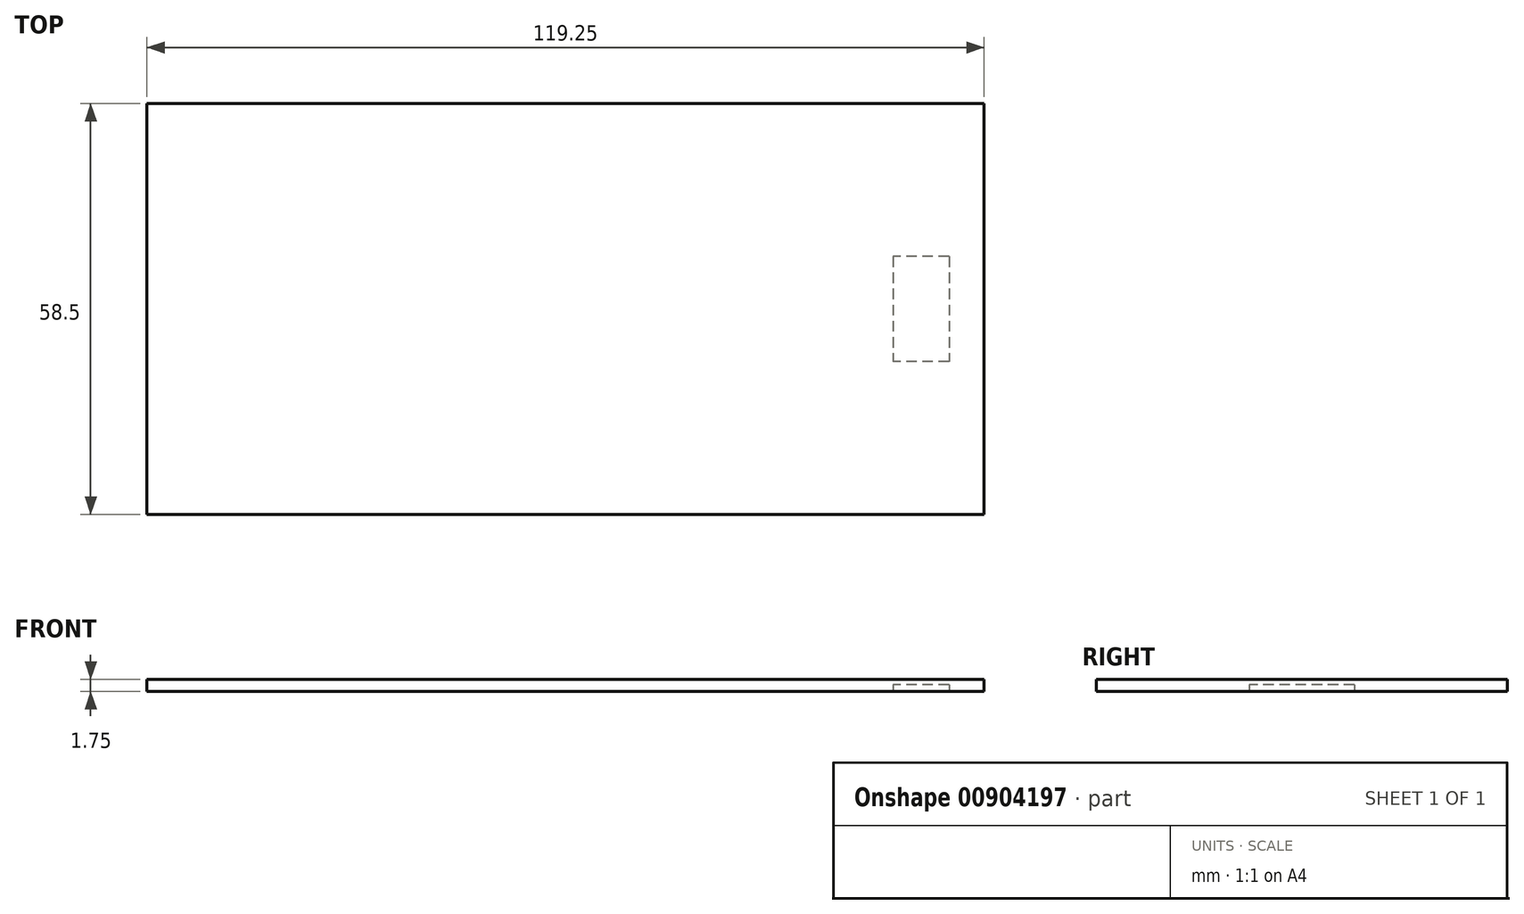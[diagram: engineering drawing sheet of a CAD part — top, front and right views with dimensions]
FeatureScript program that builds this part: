
annotation { "Feature Type Name" : "Feature", "Feature Type Description" : "" }
export const myFeature = defineFeature(function(context is Context, id is Id, definition is map)
    precondition{}
    {
        {
            var Q0;
            Q0=qCreatedBy(makeId("Top.planeOp"),FACE);
            var sketch = newSketch(context, id + "F0", { "sketchPlane" : qUnion([Q0])});
            skLineSegment(sketch, "E0.bottom", {"start": v(0, 0) * mm, "end": v(-119.25, 0) * mm});
            skLineSegment(sketch, "E0.top", {"start": v(0, -58.5) * mm, "end": v(-119.25, -58.5) * mm});
            skLineSegment(sketch, "E0.left", {"start": v(0, 0) * mm, "end": v(0, -58.5) * mm});
            skLineSegment(sketch, "E0.right", {"start": v(-119.25, 0) * mm, "end": v(-119.25, -58.5) * mm});
            skSolve(sketch);
        }
        {
            var Q0;
            Q0 = qSketchRegion(id + "F0", true);
            extrude(context, id + "F1", {"entities" : qUnion([Q0]), "depth" : 1.75 * mm, "offsetDistance" : 25 * mm});
        }
        {
            var Q0;
            Q0=qCreatedBy(makeId("Top.planeOp"),FACE);
            var sketch = newSketch(context, id + "F2", { "sketchPlane" : qUnion([Q0])});
            skLineSegment(sketch, "E1", {"start": v(0, 0) * mm, "end": v(0, -58.5) * mm});
            skLineSegment(sketch, "E2", {"start": v(0, -29.25) * mm, "end": v(-9, -29.25) * mm});
            skLineSegment(sketch, "E3.bottom", {"start": v(-5, -21.75) * mm, "end": v(-13, -21.75) * mm});
            skLineSegment(sketch, "E3.top", {"start": v(-5, -36.75) * mm, "end": v(-13, -36.75) * mm});
            skLineSegment(sketch, "E3.left", {"start": v(-5, -21.75) * mm, "end": v(-5, -36.75) * mm});
            skLineSegment(sketch, "E3.right", {"start": v(-13, -21.75) * mm, "end": v(-13, -36.75) * mm});
            skPoint(sketch, "E3.middle", {"position": v(-9, -29.25) * mm});
            skSolve(sketch);
        }
        {
            var Q0;
            Q0 = qSketchRegion(id + "F2", true);
            extrude(context, id + "F3", {"entities" : qUnion([Q0]), "operationType" : NewBodyOperationType.REMOVE, "depth" : 1 * mm, "offsetDistance" : 25 * mm});
        }
    });
